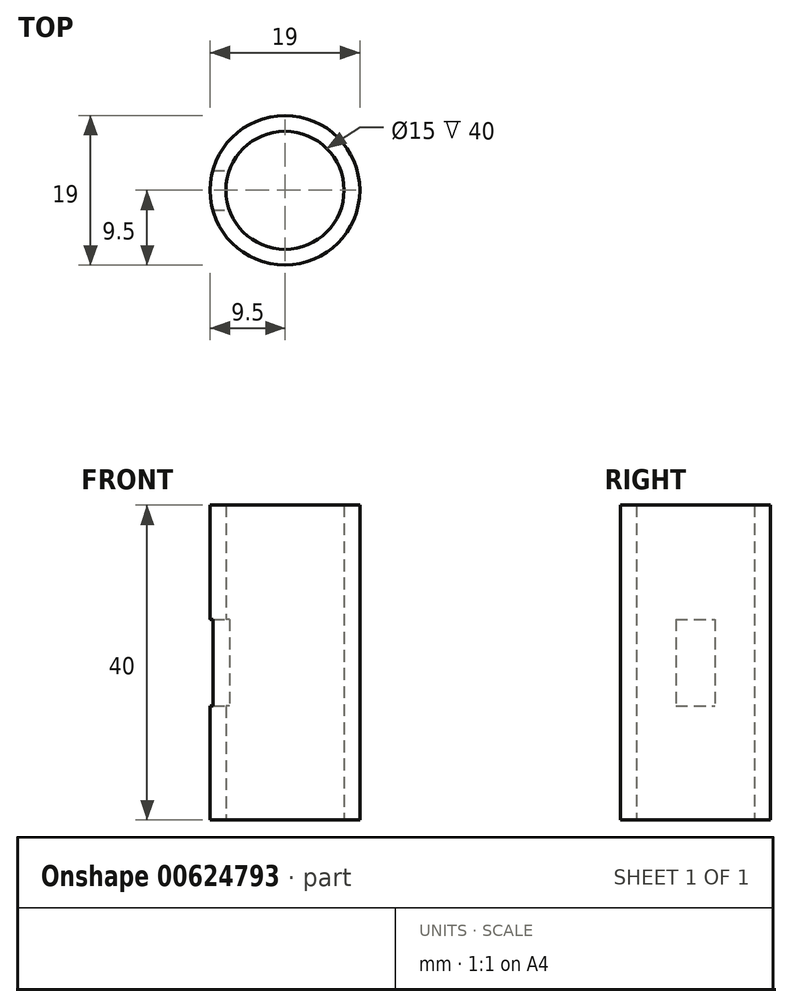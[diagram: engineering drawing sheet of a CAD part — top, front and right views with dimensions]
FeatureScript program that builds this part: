
annotation { "Feature Type Name" : "Feature", "Feature Type Description" : "" }
export const myFeature = defineFeature(function(context is Context, id is Id, definition is map)
    precondition{}
    {
        {
            var Q0;
            Q0=qCreatedBy(makeId("Top.planeOp"),FACE);
            var sketch = newSketch(context, id + "F0", { "sketchPlane" : qUnion([Q0])});
            skCircle(sketch, "E0", {"center": v(0, 0) * mm, "radius": 7.5 * mm});
            skCircle(sketch, "E1.0", {"center": v(0, 0) * mm, "radius": 9.5 * mm});
            skSolve(sketch);
        }
        {
            var Q0;
            Q0=makeQuery(id+"F0.imprint","IMPRINT",FACE,{"disambiguationData":[TD([[makeQuery(id+"F0.imprint","IMPRINT",EDGE,{"derivedFrom":sQuery(id+"F0.wireOp",EDGE,"E0")}),-1.0]])]});
            extrude(context, id + "F1", {"entities" : qUnion([Q0]), "depth" : 40 * mm, "offsetDistance" : 25 * mm});
        }
        {
            var Q0;
            Q0=qCreatedBy(makeId("Right.planeOp"),FACE);
            var sketch = newSketch(context, id + "F2", { "sketchPlane" : qUnion([Q0])});
            skLineSegment(sketch, "E2.bottom", {"start": v(-2.5, 25.5) * mm, "end": v(2.5, 25.5) * mm});
            skLineSegment(sketch, "E2.top", {"start": v(-2.5, 14.5) * mm, "end": v(2.5, 14.5) * mm});
            skLineSegment(sketch, "E2.left", {"start": v(-2.5, 25.5) * mm, "end": v(-2.5, 14.5) * mm});
            skLineSegment(sketch, "E2.right", {"start": v(2.5, 25.5) * mm, "end": v(2.5, 14.5) * mm});
            skLineSegment(sketch, "E3", {"start": v(-17, 20) * mm, "end": v(16.98, 20) * mm, "construction": true});
            skSolve(sketch);
        }
        {
            var Q0;
            Q0=qSketchRegion(id+"F2",true);
            extrude(context, id + "F3", {"entities" : qUnion([Q0]), "operationType" : NewBodyOperationType.REMOVE, "oppositeDirection" : true, "depth" : 25 * mm, "offsetDistance" : 25 * mm});
        }
    });
